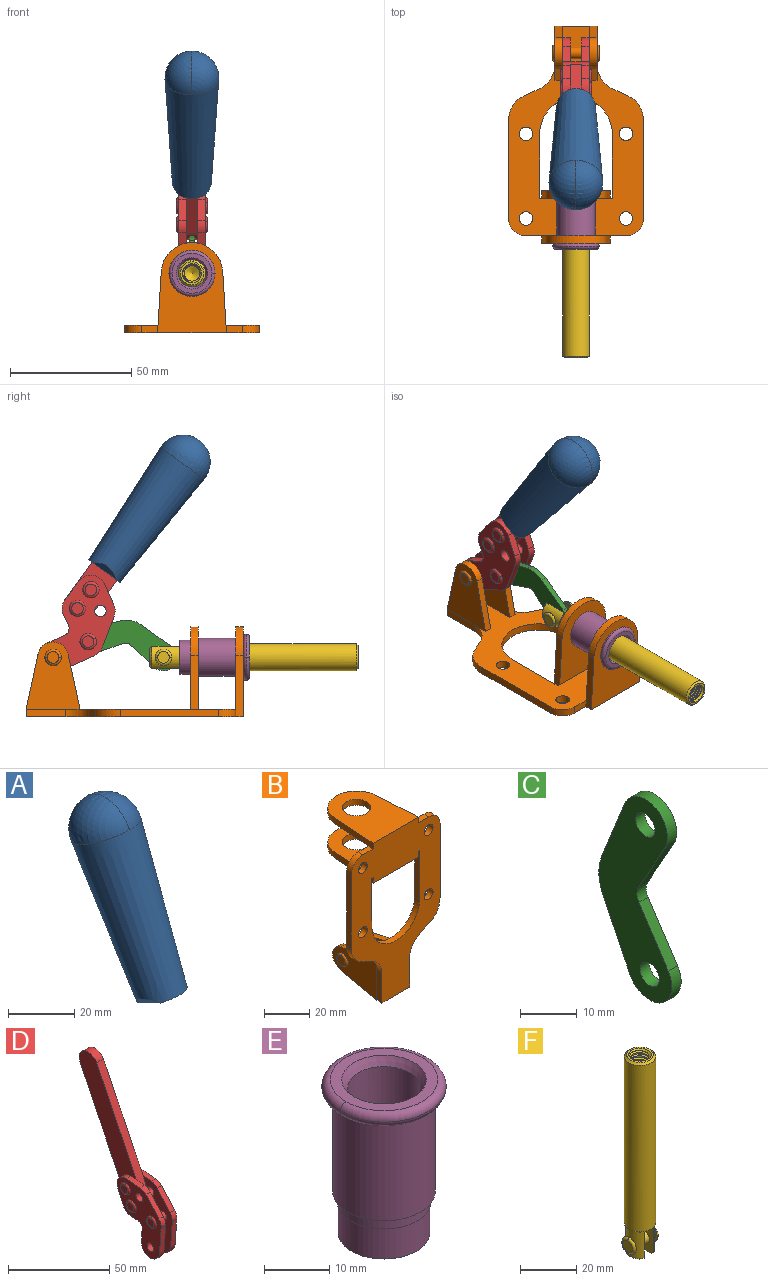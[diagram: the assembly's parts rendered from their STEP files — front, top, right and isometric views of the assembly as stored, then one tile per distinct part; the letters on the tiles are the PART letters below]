
ASSEMBLY  parts=6 mates=6
PART A: 11 faces, bbox 22.3x42.6x64.5 mm
  f0: sphere r=11.13mm, area 411.4mm2, adj f1,f8
  f1: cone r=11.11mm half-angle=3.3deg, axis (0,0.44,0.9), area 3251.8mm2, adj f0,f7,f8,f9,f10
  f2: cylinder r=6.16mm len=11.7mm, axis (1,0,0), area 89.5mm2, adj f3,f4,f5,f6
  f3: plane 60.23x36.75mm, normal (-1,0,0), area 763.6mm2, adj f2,f4,f6,f10
  f4: plane 51.37x25.05mm, normal (0,0.9,-0.44), area 264.2mm2, adj f2,f3,f5,f10
  f5: plane 60.23x36.75mm, normal (1,0,0), area 763.6mm2, adj f2,f4,f6,f10
  f6: plane 51.37x25.05mm, normal (0,-0.9,0.44), area 264.2mm2, adj f2,f3,f5,f10
  f7: plane 9.95x5.95mm, normal (0.71,-0.31,-0.64), area 25.8mm2, adj f1,f10
  f8: sphere r=11.13mm, area 411.4mm2, adj f0,f1
  f9: plane 9.95x5.95mm, normal (-0.71,-0.31,-0.64), area 25.8mm2, adj f1,f10
  f10: plane 14.27x11.38mm, normal (0,-0.44,-0.9), area 106.7mm2, adj f1,f3,f4,f5,f6,f7,f9
PART B: 55 faces, bbox 55.7x37.4x89.8 mm
  f0: torus R=2.41mm, axis (-1,0,0), area 15mm2, adj f11,f15,f25
  f1: torus R=2.41mm, axis (-1,0,0), area 15mm2, adj f10,f12,f22
  f2: cylinder r=2.78mm len=5.56mm, axis (0,-1,0), area 54.2mm2, adj f30,f54
  f3: cylinder r=14.99mm len=29.97mm, axis (0,-1,0), area 145.9mm2, adj f30,f49,f53,f54
  f4: cylinder r=2.78mm len=5.56mm, axis (0,-1,0), area 54.2mm2, adj f30,f54
  f5: cylinder r=2.78mm len=5.56mm, axis (0,-1,0), area 54.2mm2, adj f30,f54
  f6: cylinder r=2.78mm len=5.56mm, axis (0,-1,0), area 54.2mm2, adj f30,f54
  f7: cylinder r=6.35mm len=12.7mm, axis (0,0,1), area 123.6mm2, adj f27,f51
  f8: cylinder r=6.35mm len=12.7mm, axis (0,0,-1), area 124.7mm2, adj f21,f35
  f9: cylinder r=2.41mm len=11.18mm, axis (-1,0,0), area 169.4mm2, adj f16,f19
  f10: plane 4.83x4.83mm, normal (1,0,0), area 18.3mm2, adj f1,f12
  f11: plane 4.83x4.83mm, normal (-1,0,0), area 18.3mm2, adj f0,f15
  f12: torus R=2.41mm, axis (-1,0,0), area 15mm2, adj f1,f10,f22
  f13: cylinder r=6.35mm len=12.41mm, axis (1,0,0), area 53.4mm2, adj f18,f19,f22,f23
  f14: cylinder r=6.35mm len=12.41mm, axis (-1,0,0), area 53.4mm2, adj f16,f17,f24,f25
  f15: torus R=2.41mm, axis (-1,0,0), area 15mm2, adj f0,f11,f25
  f16: plane 27.86x22.35mm, normal (1,0,0), area 425.4mm2, adj f9,f14,f17,f24,f30
  f17: plane 22.86x4.97mm, normal (0,0.21,0.98), area 72.5mm2, adj f14,f16,f25,f30
  f18: plane 22.86x4.97mm, normal (0,0.21,0.98), area 72.5mm2, adj f13,f19,f22,f30
  f19: plane 27.86x22.35mm, normal (-1,0,0), area 425.4mm2, adj f9,f13,f18,f23,f30
  f20: cylinder r=12.7mm len=25.35mm, axis (0,0,-1), area 119.8mm2, adj f21,f34,f35,f36
  f21: plane 34.21x28.07mm, normal (0,0,-1), area 702.4mm2, adj f8,f20,f30,f34,f36
  f22: plane 27.96x22.45mm, normal (1,0,0), area 407.2mm2, adj f1,f12,f13,f18,f23,f30,f42,f43
  f23: plane 22.86x4.97mm, normal (0,0.21,-0.98), area 72.5mm2, adj f13,f19,f22,f44
  f24: plane 22.86x4.97mm, normal (0,0.21,-0.98), area 72.5mm2, adj f14,f16,f25,f44
  f25: plane 27.86x22.35mm, normal (-1,0,0), area 407.1mm2, adj f0,f14,f15,f17,f24,f30,f45,f46
  f26: plane 3.1x0.95mm, normal (0,0,-1), area 2.7mm2, adj f30,f49,f50,f54
  f27: plane 34.21x28.07mm, normal (0,0,1), area 702.4mm2, adj f7,f28,f30,f50,f52
  f28: cylinder r=12.7mm len=25.35mm, axis (0,0,1), area 118.8mm2, adj f27,f50,f51,f52
  f29: plane 3.1x0.95mm, normal (0,0,-1), area 2.7mm2, adj f30,f52,f53,f54
  f30: plane 86.54x55.63mm, normal (0,1,0), area 2362.9mm2, adj f2,f3,f4,f5,f6,f16,f17,f18
  f31: plane 40.56x3.1mm, normal (-1,0,0), area 125.7mm2, adj f30,f32,f48,f54
  f32: cylinder r=7.11mm len=7.11mm, axis (0,-1,0), area 34.6mm2, adj f30,f31,f33,f54
  f33: plane 6.67x3.1mm, normal (0,0,1), area 20.4mm2, adj f30,f32,f34,f54
  f34: plane 25.39x3.13mm, normal (-1,0.06,0), area 79.5mm2, adj f20,f21,f33,f35,f54
  f35: plane 37.31x28.45mm, normal (0,0,1), area 789.9mm2, adj f8,f20,f34,f36,f54
  f36: plane 25.39x3.13mm, normal (1,0.06,0), area 79.5mm2, adj f20,f21,f35,f37,f54
  f37: plane 6.67x3.1mm, normal (0,0,1), area 20.4mm2, adj f30,f36,f38,f54
  f38: cylinder r=7.11mm len=7.11mm, axis (0,-1,0), area 34.6mm2, adj f30,f37,f39,f54
  f39: plane 40.56x3.1mm, normal (1,0,0), area 125.7mm2, adj f30,f38,f40,f54
  f40: cylinder r=11.18mm len=10.16mm, axis (0,-1,0), area 39.5mm2, adj f30,f39,f41,f54
  f41: plane 6.09x3.1mm, normal (0.42,0,-0.91), area 20.8mm2, adj f30,f40,f42,f54
  f42: cylinder r=11.18mm len=9.41mm, axis (0,-1,0), area 37.2mm2, adj f22,f30,f41,f43,f54
  f43: plane 16.5x3.1mm, normal (1,0,0), area 51.1mm2, adj f22,f42,f44,f54
  f44: plane 17.37x3.1mm, normal (0,0,-1), area 53.8mm2, adj f23,f24,f30,f43,f45,f54
  f45: plane 16.5x3.1mm, normal (-1,0,0), area 51.1mm2, adj f25,f44,f46,f54
  f46: cylinder r=11.18mm len=9.41mm, axis (0,-1,0), area 37.2mm2, adj f25,f30,f45,f47,f54
  f47: plane 6.09x3.1mm, normal (-0.42,0,-0.91), area 20.8mm2, adj f30,f46,f48,f54
  f48: cylinder r=11.18mm len=10.16mm, axis (0,-1,0), area 39.5mm2, adj f30,f31,f47,f54
  f49: plane 26.54x3.1mm, normal (-1,0,0), area 82.3mm2, adj f3,f26,f30,f54
  f50: plane 25.39x3.1mm, normal (1,0.06,0), area 78.8mm2, adj f26,f27,f28,f51,f54
  f51: plane 37.31x28.45mm, normal (0,0,-1), area 789.9mm2, adj f7,f28,f50,f52,f54
  f52: plane 25.39x3.1mm, normal (-1,0.06,0), area 78.8mm2, adj f27,f28,f29,f51,f54
  f53: plane 26.54x3.1mm, normal (1,0,0), area 82.3mm2, adj f3,f29,f30,f54
  f54: plane 89.66x55.63mm, normal (0,-1,0), area 2678.5mm2, adj f2,f3,f4,f5,f6,f26,f29,f31
PART C: 12 faces, bbox 2.3x18.2x42.8 mm
  f0: cylinder r=2.4mm len=4.8mm, axis (1,0,0), area 34.9mm2, adj f4,f11
  f1: cylinder r=10.41mm len=8.47mm, axis (1,0,0), area 20.2mm2, adj f4,f9,f10,f11
  f2: cylinder r=3.05mm len=3.16mm, axis (1,0,0), area 7.7mm2, adj f4,f6,f7,f11
  f3: cylinder r=2.4mm len=4.8mm, axis (1,0,0), area 34.9mm2, adj f4,f11
  f4: plane 42.81x18.23mm, normal (-1,0,0), area 414.1mm2, adj f0,f1,f2,f3,f5,f6,f7,f8
  f5: cylinder r=5.54mm len=10.67mm, axis (1,0,0), area 41.8mm2, adj f4,f6,f10,f11
  f6: plane 11.66x6.53mm, normal (0,-0.87,-0.49), area 30.9mm2, adj f2,f4,f5,f11
  f7: plane 11.17x7.33mm, normal (0,-0.84,0.55), area 30.9mm2, adj f2,f4,f8,f11
  f8: cylinder r=5.54mm len=10.51mm, axis (1,0,0), area 41.8mm2, adj f4,f7,f9,f11
  f9: plane 13.67x6.67mm, normal (0,0.9,-0.44), area 35.1mm2, adj f1,f4,f8,f11
  f10: plane 14.1x5.7mm, normal (0,0.93,0.37), area 35.1mm2, adj f1,f4,f5,f11
  f11: plane 42.81x18.23mm, normal (1,0,0), area 414.1mm2, adj f0,f1,f2,f3,f5,f6,f7,f8
PART D: 59 faces, bbox 12.9x60.2x99.6 mm
  f0: torus R=2.39mm, axis (-1,0,0), area 14.9mm2, adj f20,f43,f51
  f1: torus R=2.39mm, axis (-1,0,0), area 14.9mm2, adj f19,f42,f51
  f2: torus R=2.39mm, axis (-1,0,0), area 14.9mm2, adj f18,f35,f51
  f3: torus R=2.39mm, axis (-1,0,0), area 14.9mm2, adj f14,f17,f23
  f4: torus R=2.39mm, axis (-1,0,0), area 14.9mm2, adj f13,f16,f23
  f5: torus R=2.39mm, axis (-1,0,0), area 14.9mm2, adj f12,f15,f23
  f6: cylinder r=2.39mm len=4.78mm, axis (1,0,0), area 46.5mm2, adj f48,f50,f51
  f7: cylinder r=2.39mm len=4.78mm, axis (1,0,0), area 46.5mm2, adj f50,f51
  f8: cylinder r=6.35mm len=12.68mm, axis (1,0,0), area 61.8mm2, adj f38,f39,f50,f51
  f9: cylinder r=2.39mm len=4.78mm, axis (-1,0,0), area 70.5mm2, adj f46,f50
  f10: cylinder r=2.39mm len=4.78mm, axis (-1,0,0), area 46.5mm2, adj f23,f45,f46
  f11: cylinder r=2.39mm len=4.78mm, axis (-1,0,0), area 46.5mm2, adj f23,f46
  f12: plane 4.78x4.78mm, normal (1,0,0), area 17.9mm2, adj f5,f15
  f13: plane 4.78x4.78mm, normal (1,0,0), area 17.9mm2, adj f4,f16
  f14: plane 4.78x4.78mm, normal (1,0,0), area 17.9mm2, adj f3,f17
  f15: torus R=2.39mm, axis (-1,0,0), area 14.9mm2, adj f5,f12,f23
  f16: torus R=2.39mm, axis (-1,0,0), area 14.9mm2, adj f4,f13,f23
  f17: torus R=2.39mm, axis (-1,0,0), area 14.9mm2, adj f3,f14,f23
  f18: plane 4.78x4.78mm, normal (-1,0,0), area 17.9mm2, adj f2,f35
  f19: plane 4.78x4.78mm, normal (-1,0,0), area 17.9mm2, adj f1,f42
  f20: plane 4.78x4.78mm, normal (-1,0,0), area 17.9mm2, adj f0,f43
  f21: plane 2.26x0.2mm, normal (1,0,0), area 0.2mm2, adj f31,f44
  f22: plane 2.26x0.2mm, normal (-1,0,0), area 0.2mm2, adj f41,f44
  f23: plane 39.37x30.77mm, normal (1,0,0), area 565.5mm2, adj f3,f4,f5,f10,f11,f15,f16,f17
  f24: cylinder r=6.1mm len=4.15mm, axis (-1,0,0), area 14.7mm2, adj f23,f25,f32,f46
  f25: plane 10.25x9.01mm, normal (0,-0.75,0.66), area 42.3mm2, adj f23,f24,f26,f46
  f26: cylinder r=6.35mm len=4.64mm, axis (-1,0,0), area 15.6mm2, adj f23,f25,f27,f46
  f27: plane 15.84x3.1mm, normal (0,-1,-0.07), area 49.2mm2, adj f23,f26,f28,f46
  f28: cylinder r=6.35mm len=12.68mm, axis (-1,0,0), area 61.8mm2, adj f23,f27,f29,f46
  f29: plane 8.11x3.1mm, normal (0,1,0.07), area 25.2mm2, adj f23,f28,f30,f46
  f30: cylinder r=3.05mm len=3.25mm, axis (-1,0,0), area 14.8mm2, adj f23,f29,f31,f46
  f31: plane 5.99x3.1mm, normal (0,0.07,-1), area 18.6mm2, adj f21,f23,f30,f44,f46
  f32: plane 9.5x3.1mm, normal (0,-0.07,1), area 29.5mm2, adj f23,f24,f33,f46,f47
  f33: cylinder r=6.1mm len=8.63mm, axis (-1,0,0), area 39.1mm2, adj f23,f32,f34,f47
  f34: plane 8.65x3.96mm, normal (0,0.91,-0.42), area 29.5mm2, adj f23,f33,f44,f47
  f35: torus R=2.39mm, axis (-1,0,0), area 14.9mm2, adj f2,f18,f51
  f36: plane 10.25x9.01mm, normal (0,-0.75,0.66), area 42.3mm2, adj f37,f49,f50,f51
  f37: cylinder r=6.35mm len=4.64mm, axis (1,0,0), area 15.6mm2, adj f36,f38,f50,f51
  f38: plane 15.84x3.1mm, normal (0,-1,-0.07), area 49.2mm2, adj f8,f37,f50,f51
  f39: plane 8.11x3.1mm, normal (0,1,0.07), area 25.2mm2, adj f8,f40,f50,f51
  f40: cylinder r=3.05mm len=3.25mm, axis (1,0,0), area 14.8mm2, adj f39,f41,f50,f51
  f41: plane 5.99x3.1mm, normal (0,0.07,-1), area 18.6mm2, adj f22,f40,f44,f50,f51
  f42: torus R=2.39mm, axis (-1,0,0), area 14.9mm2, adj f1,f19,f51
  f43: torus R=2.39mm, axis (-1,0,0), area 14.9mm2, adj f0,f20,f51
  f44: cylinder r=6.35mm len=12.12mm, axis (-1,0,0), area 128.9mm2, adj f21,f22,f23,f31,f34,f41,f46,f47
  f45: plane 2.65x1.35mm, normal (1,0,0), area 1mm2, adj f10,f55
  f46: plane 39.08x20.42mm, normal (-1,0,0), area 412.5mm2, adj f9,f10,f11,f24,f25,f26,f27,f28
  f47: plane 77.62x39.82mm, normal (1,0,0), area 850mm2, adj f32,f33,f34,f44,f53,f54,f55
  f48: plane 2.65x1.35mm, normal (-1,0,0), area 1mm2, adj f6,f55
  f49: cylinder r=6.1mm len=4.15mm, axis (1,0,0), area 14.7mm2, adj f36,f50,f51,f56
  f50: plane 39.08x20.42mm, normal (1,0,0), area 412.5mm2, adj f6,f7,f8,f9,f36,f37,f38,f39
  f51: plane 39.37x30.77mm, normal (-1,0,0), area 565.5mm2, adj f0,f1,f2,f6,f7,f8,f35,f36
  f52: plane 8.65x3.96mm, normal (0,0.91,-0.42), area 29.5mm2, adj f44,f51,f57,f58
  f53: plane 68.49x33.4mm, normal (0,0.9,-0.44), area 358.1mm2, adj f44,f47,f54,f58
  f54: cylinder r=6.35mm len=12.06mm, axis (1,0,0), area 93.7mm2, adj f47,f53,f55,f58
  f55: plane 68.49x33.4mm, normal (0,-0.9,0.44), area 358.1mm2, adj f44,f45,f46,f47,f48,f50,f54,f58
  f56: plane 9.5x3.1mm, normal (0,-0.07,1), area 29.5mm2, adj f49,f50,f51,f57,f58
  f57: cylinder r=6.1mm len=8.63mm, axis (1,0,0), area 39.1mm2, adj f51,f52,f56,f58
  f58: plane 77.62x39.82mm, normal (-1,0,0), area 850mm2, adj f44,f52,f53,f54,f55,f56,f57
PART E: 15 faces, bbox 20.6x20.6x28.7 mm
  f0: torus R=8.26mm, axis (0,0,1), area 56.8mm2, adj f1,f10,f12
  f1: torus R=8.26mm, axis (0,0,1), area 56.8mm2, adj f0,f6,f13
  f2: cylinder r=5.59mm len=25.91mm, axis (0,0,1), area 909.6mm2, adj f3,f4
  f3: cone r=6.86mm half-angle=45deg, axis (0,0,-1), area 70.2mm2, adj f2,f14
  f4: cone r=6.47mm half-angle=30deg, axis (0,0,1), area 66.7mm2, adj f2,f13
  f5: cylinder r=7.04mm len=14.07mm, axis (0,0,1), area 252.6mm2, adj f11,f14
  f6: torus R=8.26mm, axis (0,0,1), area 56.8mm2, adj f1,f12,f13
  f7: cylinder r=7.16mm len=14.33mm, axis (0,0,1), area 91.5mm2, adj f9,f11
  f8: cylinder r=7.86mm len=18.42mm, axis (0,0,1), area 909.6mm2, adj f9,f10
  f9: plane 15.72x15.72mm, normal (0,0,-1), area 33mm2, adj f7,f8
  f10: plane 16.51x16.51mm, normal (0,0,-1), area 19.9mm2, adj f0,f8,f12
  f11: plane 14.33x14.33mm, normal (0,0,-1), area 5.7mm2, adj f5,f7
  f12: torus R=8.26mm, axis (0,0,1), area 56.8mm2, adj f0,f6,f10
  f13: plane 16.51x16.51mm, normal (0,0,1), area 82.7mm2, adj f1,f4,f6
  f14: plane 14.07x14.07mm, normal (0,0,-1), area 7.8mm2, adj f3,f5
PART F: 48 faces, bbox 12.6x11.1x86.1 mm
  f0: torus R=2.41mm, axis (-1,0,0), area 15mm2, adj f30,f32,f34
  f1: torus R=2.41mm, axis (-1,0,0), area 15mm2, adj f29,f31,f33
  f2: cylinder r=5.54mm len=72.39mm, axis (0,0,1), area 2518.5mm2, adj f3,f4,f42,f43
  f3: cone r=5.54mm half-angle=45deg, axis (0,0,1), area 7.6mm2, adj f2,f5,f41
  f4: cone r=5.54mm half-angle=45deg, axis (0,0,-1), area 34.9mm2, adj f2,f39
  f5: cylinder r=5.08mm len=11.48mm, axis (0,0,1), area 108.3mm2, adj f3,f7,f8,f41
  f6: cylinder r=2.41mm len=4.83mm, axis (-1,0,0), area 71.2mm2, adj f40,f41
  f7: cylinder r=2.41mm len=4.83mm, axis (-1,0,0), area 7.6mm2, adj f5,f34
  f8: cone r=5.08mm half-angle=45deg, axis (0,0,1), area 10.6mm2, adj f5,f37,f41
  f9: cone r=3.98mm half-angle=45deg, axis (0,0,1), area 17.6mm2, adj f27,f39,f45,f46,f47
  f10: cylinder r=2.41mm len=4.83mm, axis (-1,0,0), area 7.6mm2, adj f33,f38
  f11: cylinder r=3.2mm len=6.4mm, axis (0,0,1), area 78.4mm2, adj f12,f28,f44,f45,f47
  f12: cylinder r=3.2mm len=6.4mm, axis (0,0,1), area 10.5mm2, adj f11,f13,f45,f47
  f13: cylinder r=3.2mm len=6.4mm, axis (0,0,1), area 10.5mm2, adj f12,f14,f45,f47
  f14: cylinder r=3.2mm len=6.4mm, axis (0,0,1), area 10.5mm2, adj f13,f15,f45,f47
  f15: cylinder r=3.2mm len=6.4mm, axis (0,0,1), area 10.5mm2, adj f14,f16,f45,f47
  f16: cylinder r=3.2mm len=6.4mm, axis (0,0,1), area 10.5mm2, adj f15,f17,f45,f47
  f17: cylinder r=3.2mm len=6.4mm, axis (0,0,1), area 10.5mm2, adj f16,f18,f45,f47
  f18: cylinder r=3.2mm len=6.4mm, axis (0,0,1), area 10.5mm2, adj f17,f19,f45,f47
  f19: cylinder r=3.2mm len=6.4mm, axis (0,0,1), area 10.5mm2, adj f18,f20,f45,f47
  f20: cylinder r=3.2mm len=6.4mm, axis (0,0,1), area 10.5mm2, adj f19,f21,f45,f47
  f21: cylinder r=3.2mm len=6.4mm, axis (0,0,1), area 10.5mm2, adj f20,f22,f45,f47
  f22: cylinder r=3.2mm len=6.4mm, axis (0,0,1), area 10.5mm2, adj f21,f23,f45,f47
  f23: cylinder r=3.2mm len=6.4mm, axis (0,0,1), area 10.5mm2, adj f22,f24,f45,f47
  f24: cylinder r=3.2mm len=6.4mm, axis (0,0,1), area 10.5mm2, adj f23,f25,f45,f47
  f25: cylinder r=3.2mm len=6.4mm, axis (0,0,1), area 10.5mm2, adj f24,f26,f45,f47
  f26: cylinder r=3.2mm len=6.4mm, axis (0,0,1), area 10.5mm2, adj f25,f27,f45,f47
  f27: cylinder r=3.2mm len=6.4mm, axis (0,0,1), area 7.4mm2, adj f9,f26,f45,f47
  f28: cone r=3.2mm half-angle=60deg, axis (0,0,1), area 37.2mm2, adj f11
  f29: plane 4.83x4.83mm, normal (-1,0,0), area 18.3mm2, adj f1,f31
  f30: plane 4.83x4.83mm, normal (1,0,0), area 18.3mm2, adj f0,f32
  f31: torus R=2.41mm, axis (-1,0,0), area 15mm2, adj f1,f29,f33
  f32: torus R=2.41mm, axis (-1,0,0), area 15mm2, adj f0,f30,f34
  f33: plane 6.83x6.83mm, normal (1,0,0), area 18.3mm2, adj f1,f10,f31
  f34: plane 6.83x6.83mm, normal (-1,0,0), area 18.3mm2, adj f0,f7,f32
  f35: cone r=5.08mm half-angle=45deg, axis (0,0,1), area 10.6mm2, adj f36,f38,f40
  f36: plane 7.25x1.97mm, normal (0,0,-1), area 10mm2, adj f35,f40
  f37: plane 7.25x1.97mm, normal (0,0,-1), area 10mm2, adj f8,f41
  f38: cylinder r=5.08mm len=11.48mm, axis (0,0,1), area 108.3mm2, adj f10,f35,f40,f42
  f39: plane 9.55x9.55mm, normal (0,0,1), area 22mm2, adj f4,f9
  f40: plane 12.76x10.09mm, normal (1,0,0), area 95.7mm2, adj f6,f35,f36,f38,f42,f43
  f41: plane 12.76x10.09mm, normal (-1,0,0), area 95.7mm2, adj f3,f5,f6,f8,f37,f43
  f42: cone r=5.54mm half-angle=45deg, axis (0,0,1), area 7.6mm2, adj f2,f38,f40
  f43: plane 11.07x4.7mm, normal (0,0,-1), area 50.4mm2, adj f2,f40,f41
  f44: plane 0.89x0.62mm, normal (-1,0,0), area 0.3mm2, adj f11,f45,f46,f47
  f45: bspline ~24.8x7.63mm, area 266.6mm2, adj f9,f11,f12,f13,f14,f15,f16,f17
  f46: bspline ~24.87x7.63mm, area 73.6mm2, adj f9,f44,f45,f47
  f47: bspline ~24.98x7.63mm, area 272.5mm2, adj f9,f11,f12,f13,f14,f15,f16,f17
PLACE A rot(axis=(1,0,0),61.8deg) t=(-0.04,1.32,18.06)mm
PLACE B rot(axis=(1,0,0),90deg) t=(0,9.14,0)mm fixed
PLACE C rot(axis=(0,-0.64,-0.76),180deg) t=(0,15.69,4.22)mm
PLACE D rot(axis=(1,0,0),61.8deg) t=(0,1.32,18.06)mm
PLACE E rot(axis=(1,0,0),90deg) t=(0,9.14,0)mm
PLACE F rot(axis=(1,0,0),90deg) t=(0,11.14,0)mm
MATE fastened E.f2 <-> B.f7  axis (0,1,0) through (0,-37.25,24.61)mm
MATE fastened A.f2 <-> D.f54  axis (1,0,0) through (-2.35,-13.44,106.54)mm
MATE revolute B.f0 <-> D.f7  axis (-1,0,0) through (0,41.23,24.61)mm
MATE revolute F.f6 <-> C.f3  axis (-1,0,0) through (0,-4.33,24.61)mm
MATE slider F.f2 <-> B.f7  axis (0,-1,0) through (0,-47.64,24.61)mm
MATE revolute C.f5 <-> D.f4  axis (-1,0,0) through (0,26.75,31.11)mm
